# Revit family: xBasin-Above_Counter-American_Standard-Townsend-0329_Series
name_source: partatom
category: Plumbing Fixtures
revit_build: Autodesk Revit 2014 (Build: 20130308_1515(x64)
units: mm (PartAtom-declared; Revit-internal decimal feet)

## types (3) — shared parameters
Assembly Code = D2010310
Basin Shape = Rectangular
CW Connection = Yes
CWFU = 1.5
Cold Water Connection Diameter = 1/2"
Cold Water Connection Height = 20 1/4"
Cold Water Connection Radius = 1/4"
Cold Water Connection Width = 4"
Default Elevation = 31"
Description = Townsend Above-Counter Rectangular Sink
HW Connection = Yes
HWFU = 1.5
Height = 7 1/8"
Hot Water Connection Diameter = 1"
Hot Water Connection Height = 20 1/4"
Hot Water Connection Radius = 1/4"
Hot Water Connection Width = 4"
Installation Type = Above-Counter
Length = 18"
Manufacturer = American Standard
Material = Fine-American_Standard-Fireclay
Price = Prices may vary. Please consult Manufacturer Representative for most up-to-date price list.
URL = https://www.americanstandard-us.com
Vent Connection = No
WFU = 2
Waste Connection = Yes
Waste Connection Diameter = 1 1/4"
Waste Connection Height = 18 1/8"
Waste Connection Radius = 5/8"
Width = 24"

## per-type parameters (varying)
| type | Far Left Faucet Hole | Far Right Faucet Hole | Faucet Holes Width |
| 0329.008 | Yes | Yes | 8" |
| 0329.004 | Yes | Yes | 4" |
| 0329.001 | No | No | 35" |

note: column(s) folded — value = type name in every type: Model

## geometry (parser evidence)
native form markers: Sweep x1
no freeform markers — native parametric forms only
